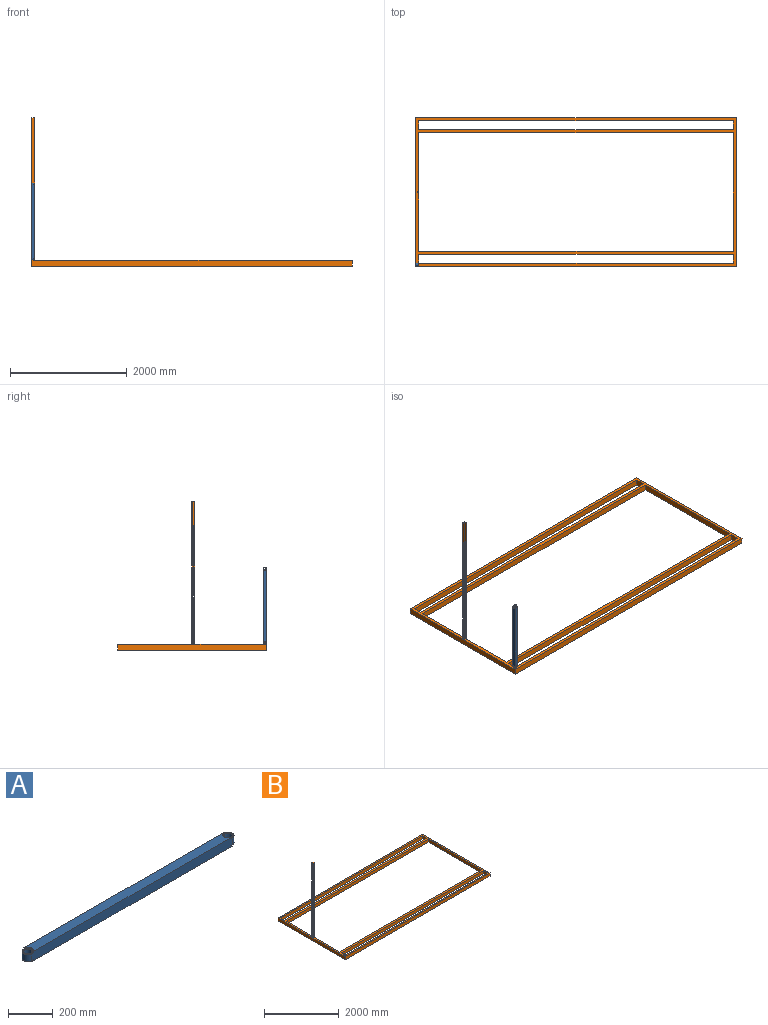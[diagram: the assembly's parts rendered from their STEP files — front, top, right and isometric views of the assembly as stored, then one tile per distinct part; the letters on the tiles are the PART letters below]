
ASSEMBLY  parts=2 mates=1
PART A: 16 faces, bbox 1320.8x50.8x50.8 mm
  f0: cylinder r=25.4mm len=50.8mm, axis (0,0,-1), area 506.7mm2, adj f3,f5,f7,f13
  f1: cylinder r=25.4mm len=50.8mm, axis (0,0,-1), area 506.7mm2, adj f3,f5,f7,f10
  f2: cylinder r=25.4mm len=50.8mm, axis (0,0,-1), area 506.7mm2, adj f3,f5,f6,f12
  f3: plane 1270x50.8mm, normal (0,-1,0), area 64516mm2, adj f0,f1,f2,f4,f6,f7,f11,f14
  f4: cylinder r=25.4mm len=50.8mm, axis (0,0,-1), area 506.7mm2, adj f3,f5,f6,f9
  f5: plane 1270x50.8mm, normal (0,1,0), area 64516mm2, adj f0,f1,f2,f4,f6,f7,f11,f14
  f6: plane 1270x50.8mm, normal (0,0,1), area 62489.2mm2, adj f2,f3,f4,f5
  f7: plane 1270x50.8mm, normal (0,0,-1), area 62489.2mm2, adj f0,f1,f3,f5
  f8: cylinder r=19.05mm len=38.1mm, axis (0,0,-1), area 4560.4mm2, adj f9,f10
  f9: plane 50.8x50.8mm, normal (0,0,1), area 886.7mm2, adj f4,f8,f11
  f10: plane 50.8x50.8mm, normal (0,0,-1), area 886.7mm2, adj f1,f8,f11
  f11: cylinder r=25.4mm len=50.8mm, axis (0,0,-1), area 3040.2mm2, adj f3,f5,f9,f10
  f12: plane 50.8x50.8mm, normal (0,0,1), area 886.7mm2, adj f2,f14,f15
  f13: plane 50.8x50.8mm, normal (0,0,-1), area 886.7mm2, adj f0,f14,f15
  f14: cylinder r=25.4mm len=50.8mm, axis (0,0,-1), area 3040.2mm2, adj f3,f5,f12,f13
  f15: cylinder r=19.05mm len=38.1mm, axis (0,0,-1), area 4560.4mm2, adj f12,f13
PART B: 39 faces, bbox 5486.4x2540x2540 mm
  f0: plane 5486.4x2540mm, normal (0,0,1), area 1350884.4mm2, adj f1,f2,f3,f4,f5,f6,f7,f8
  f1: plane 2540x2032mm, normal (1,0,0), area 304515.5mm2, adj f0,f5,f6,f19,f20,f23,f24,f25
  f2: plane 2540x2540mm, normal (-1,0,0), area 358709mm2, adj f0,f10,f11,f19,f20,f21,f24,f28
  f3: plane 2438.4x44.45mm, normal (1,0,0), area 82580.5mm2, adj f0,f21,f22,f24,f28,f29,f30
  f4: plane 2438.4x44.45mm, normal (-1,0,0), area 82580.5mm2, adj f0,f22,f23,f24,f25,f26,f27
  f5: plane 5384.8x101.6mm, normal (0,1,0), area 547095.7mm2, adj f0,f1,f18,f19
  f6: plane 5384.8x101.6mm, normal (0,-1,0), area 547095.7mm2, adj f0,f1,f18,f19
  f7: plane 152.4x101.6mm, normal (1,0,0), area 15483.8mm2, adj f0,f8,f15,f19
  f8: plane 5384.8x101.6mm, normal (0,-1,0), area 547095.7mm2, adj f0,f7,f9,f19
  f9: plane 152.4x101.6mm, normal (-1,0,0), area 15483.8mm2, adj f0,f8,f15,f19
  f10: plane 5486.4x101.6mm, normal (0,1,0), area 557418.2mm2, adj f0,f2,f16,f19
  f11: plane 5486.4x152.4mm, normal (0,-1,0), area 558063.4mm2, adj f0,f2,f16,f19,f32,f33,f34,f36
  f12: plane 5384.8x101.6mm, normal (0,1,0), area 547095.7mm2, adj f0,f13,f17,f19
  f13: plane 152.4x101.6mm, normal (1,0,0), area 15483.8mm2, adj f0,f12,f14,f19
  f14: plane 5384.8x101.6mm, normal (0,-1,0), area 547095.7mm2, adj f0,f13,f17,f19
  f15: plane 5384.8x101.6mm, normal (0,1,0), area 547095.7mm2, adj f0,f7,f9,f19
  f16: plane 2540x101.6mm, normal (1,0,0), area 258064mm2, adj f0,f10,f11,f19
  f17: plane 152.4x101.6mm, normal (-1,0,0), area 15483.8mm2, adj f0,f12,f14,f19
  f18: plane 2032x101.6mm, normal (-1,0,0), area 206451.2mm2, adj f0,f5,f6,f19
  f19: plane 5486.4x2540mm, normal (0,0,-1), area 1352255.4mm2, adj f1,f2,f5,f6,f7,f8,f9,f10
  f20: plane 2438.4x50.8mm, normal (0,1,0), area 123870.7mm2, adj f0,f1,f2,f24
  f21: plane 2438.4x6.35mm, normal (0,-1,0), area 15483.8mm2, adj f0,f2,f3,f24
  f22: plane 2438.4x38.1mm, normal (0,-1,0), area 92903mm2, adj f0,f3,f4,f24
  f23: plane 2438.4x6.35mm, normal (0,-1,0), area 15483.8mm2, adj f0,f1,f4,f24
  f24: plane 50.8x50.8mm, normal (0,0,1), area 887.1mm2, adj f1,f2,f3,f4,f20,f21,f22,f23
  f25: plane 12.7x6.35mm, normal (0,0,-1), area 80.6mm2, adj f1,f4,f26,f27
  f26: plane 2032x6.35mm, normal (0,1,0), area 12903.2mm2, adj f0,f1,f4,f25
  f27: plane 2032x6.35mm, normal (0,-1,0), area 12903.2mm2, adj f0,f1,f4,f25
  f28: plane 2032x6.35mm, normal (0,-1,0), area 12903.2mm2, adj f0,f2,f3,f30
  f29: plane 2032x6.35mm, normal (0,1,0), area 12903.2mm2, adj f0,f2,f3,f30
  f30: plane 12.7x6.35mm, normal (0,0,-1), area 80.6mm2, adj f2,f3,f28,f29
  f31: plane 50.8x6.35mm, normal (0,1,0), area 322.6mm2, adj f0,f2,f32,f33
  f32: plane 50.8x50.8mm, normal (1,0,0), area 1440.5mm2, adj f0,f11,f31,f33,f38
  f33: plane 50.8x6.35mm, normal (0,0,1), area 322.6mm2, adj f2,f11,f31,f32
  f34: plane 50.8x50.8mm, normal (1,0,0), area 2580.6mm2, adj f0,f11,f35,f37
  f35: plane 50.8x6.35mm, normal (0,1,0), area 322.6mm2, adj f0,f34,f36,f37
  f36: plane 50.8x50.8mm, normal (-1,0,0), area 1440.5mm2, adj f0,f11,f35,f37,f38
  f37: plane 50.8x6.35mm, normal (0,0,1), area 322.6mm2, adj f11,f34,f35,f36
  f38: cylinder r=19.05mm len=38.1mm, axis (1,0,0), area 4560.4mm2, adj f32,f36
PLACE A rot(axis=(0,-1,0),90deg) t=(1102.55,1231.92,944.31)mm
PLACE B t=(1077.15,1261.68,-366.4)mm
MATE revolute A.f0 <-> B.f38  axis (1,0,0) through (1083.5,1287.97,-239.4)mm
